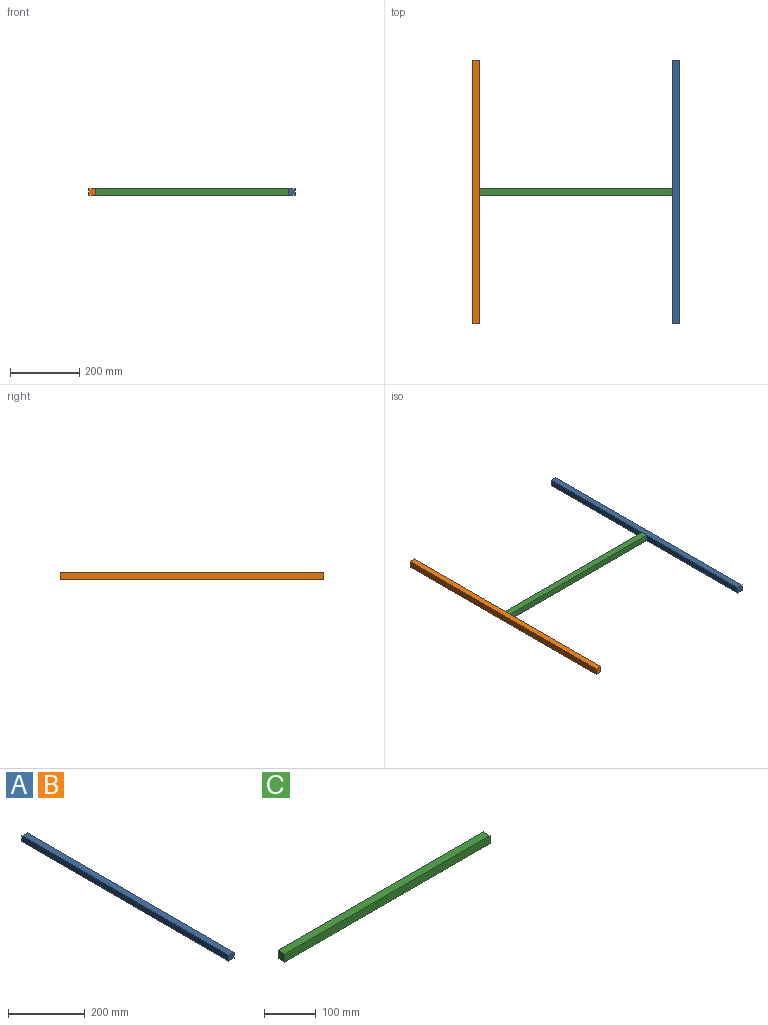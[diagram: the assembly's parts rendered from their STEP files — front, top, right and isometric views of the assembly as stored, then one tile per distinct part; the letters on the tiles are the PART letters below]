
ASSEMBLY  parts=3 mates=2
PART A: 6 faces, bbox 19.1x762x19.1 mm
  f0: plane 762x19.05mm, normal (0,0,1), area 14516.1mm2, adj f1,f3,f4,f5
  f1: plane 762x19.05mm, normal (-1,0,0), area 14516.1mm2, adj f0,f2,f4,f5
  f2: plane 762x19.05mm, normal (0,0,-1), area 14516.1mm2, adj f1,f3,f4,f5
  f3: plane 762x19.05mm, normal (1,0,0), area 14516.1mm2, adj f0,f2,f4,f5
  f4: plane 19.05x19.05mm, normal (0,-1,0), area 362.9mm2, adj f0,f1,f2,f3
  f5: plane 19.05x19.05mm, normal (0,1,0), area 362.9mm2, adj f0,f1,f2,f3
PART B: same geometry as A
PART C: 6 faces, bbox 558.8x19.1x19.1 mm
  f0: plane 558.8x19.05mm, normal (0,1,0), area 10645.1mm2, adj f1,f3,f4,f5
  f1: plane 19.05x19.05mm, normal (-1,0,0), area 362.9mm2, adj f0,f2,f4,f5
  f2: plane 558.8x19.05mm, normal (0,-1,0), area 10645.1mm2, adj f1,f3,f4,f5
  f3: plane 19.05x19.05mm, normal (1,0,0), area 362.9mm2, adj f0,f2,f4,f5
  f4: plane 558.8x19.05mm, normal (0,0,1), area 10645.1mm2, adj f0,f1,f2,f3
  f5: plane 558.8x19.05mm, normal (0,0,-1), area 10645.1mm2, adj f0,f1,f2,f3
PLACE A t=(31.23,241.75,-224.58)mm fixed
PLACE B t=(-546.62,241.75,-224.58)mm
PLACE C t=(-280.31,-128.29,-200.29)mm
MATE fastened C.f3 <-> A.f1  axis (1,0,0) through (-30.43,-139.25,-190.77)mm
MATE fastened B.f3 <-> C.f1  axis (1,0,0) through (-589.23,-139.25,-190.77)mm
